# Revit family: xFaucet-Two_Handle-American_Standard-Fluent-7186_Series
name_source: partatom
category: Plumbing Fixtures
revit_build: Autodesk Revit 2014 (Build: 20130308_1515(x64)
units: mm (PartAtom-declared; Revit-internal decimal feet)

## types (3) — shared parameters
ADA Compliant = Yes
Assembly Code = D2020300
CW Connection = Yes
CWFU = 1.5
Cold Water Connection Diameter = 1/2"
Default Elevation = 0"
Description = Fluent Two-Handle Centerset Lavatory Faucet.
Flow Rate = 1.5 GPM (5.7 L/min)
HW Connection = Yes
HWFU = 1.5
Height = 6 5/8"
Hot Water Connection Diameter = 1/2"
Installation Type = Deck Mounted
Length = 6 1/8"
Manufacturer = American Standard
Material = Metal-American Standard-002-Polished Chrome
Price = Prices may vary. Please consult Manufacturer Representative for most up-to-date price list.
Product Documentation Link = https://www.americanstandard-us.com
Product Page URL = https://www.americanstandard-us.com
Revised Date = 02/07/2017
URL = http://www.americanstandard-us.com
Vent Connection = No
Warranty Information = Limited Lifetime Function and Finish Warranty
Waste Connection = No
Width = 9 1/2"
zero-valued in all types: WFU

## per-type parameters (varying)
| type | Indicators | Specification |
| 7186.201 | No | Fluent Two-Handle Centerset. Metal Speed Connect pop-up drain. Metal lever handles. |
| 7186.203 | No | Fluent Two-Handle Centerset. Non-Metallic Speed Connect pop-up drain. Metal lever handle. |
| 7186.211 | Yes | Fluent Two-Handle Centerset Metal Speed Connect pop-up drain. Metal lever handles with red and blue indicators. |

note: column(s) folded — value = type name in every type: Model

## geometry (parser evidence)
native form markers: Sweep x1
no freeform markers — native parametric forms only
